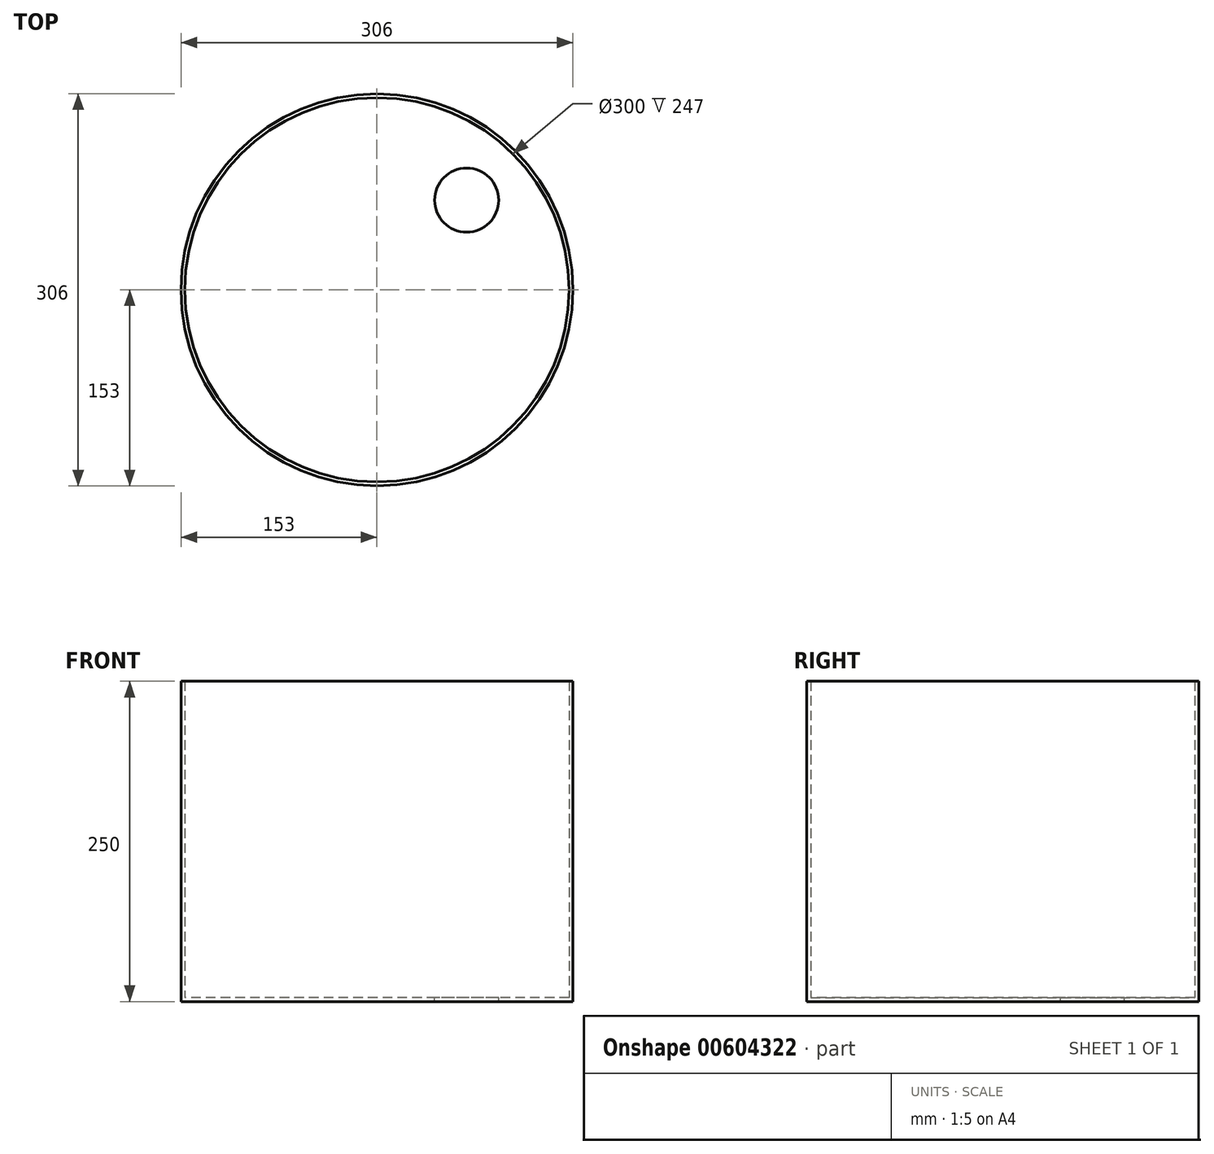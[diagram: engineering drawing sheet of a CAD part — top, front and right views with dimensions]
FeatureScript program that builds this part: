
annotation { "Feature Type Name" : "Feature", "Feature Type Description" : "" }
export const myFeature = defineFeature(function(context is Context, id is Id, definition is map)
    precondition{}
    {
        {
            var Q0;
            Q0=qCreatedBy(makeId("Top.planeOp"),FACE);
            var sketch = newSketch(context, id + "F0", { "sketchPlane" : qUnion([Q0])});
            skCircle(sketch, "E0", {"center": v(0, 0) * mm, "radius": 153 * mm});
            skSolve(sketch);
        }
        {
            var Q0;
            Q0 = qSketchRegion(id + "F0", true);
            extrude(context, id + "F1", {"entities" : qUnion([Q0]), "depth" : 250 * mm, "offsetDistance" : 25 * mm});
        }
        {
            var Q0;
            Q0=makeQuery(id+"F1.opExtrude","CAP_FACE",FACE,{"disambiguationData":[OSD([sQuery(id+"F0.wireOp",EDGE,"E0")])],"isStart":false});
            shell(context, id + "F2", {"entities" : qUnion([Q0]), "thickness" : 3 * mm});
        }
        {
            var Q0;
            {var subQ0=sQuery(id+"F0.wireOp",EDGE,"E0");Q0=makeQuery(id+"F2.opShell","OFFSET_FACE",FACE,{"disambiguationData":[OSD([subQ0]),TDD([makeQuery(id+"F1.opExtrude","CAP_FACE",FACE,{"disambiguationData":[OSD([subQ0])],"isStart":true})])]});}
            var sketch = newSketch(context, id + "F3", { "sketchPlane" : qUnion([Q0])});
            skCircle(sketch, "E1", {"center": v(70, 70) * mm, "radius": 25 * mm});
            skSolve(sketch);
        }
        {
            var Q0;
            Q0 = qSketchRegion(id + "F3", true);
            extrude(context, id + "F4", {"entities" : qUnion([Q0]), "operationType" : NewBodyOperationType.REMOVE, "oppositeDirection" : true, "depth" : 25 * mm, "offsetDistance" : 25 * mm});
        }
    });
